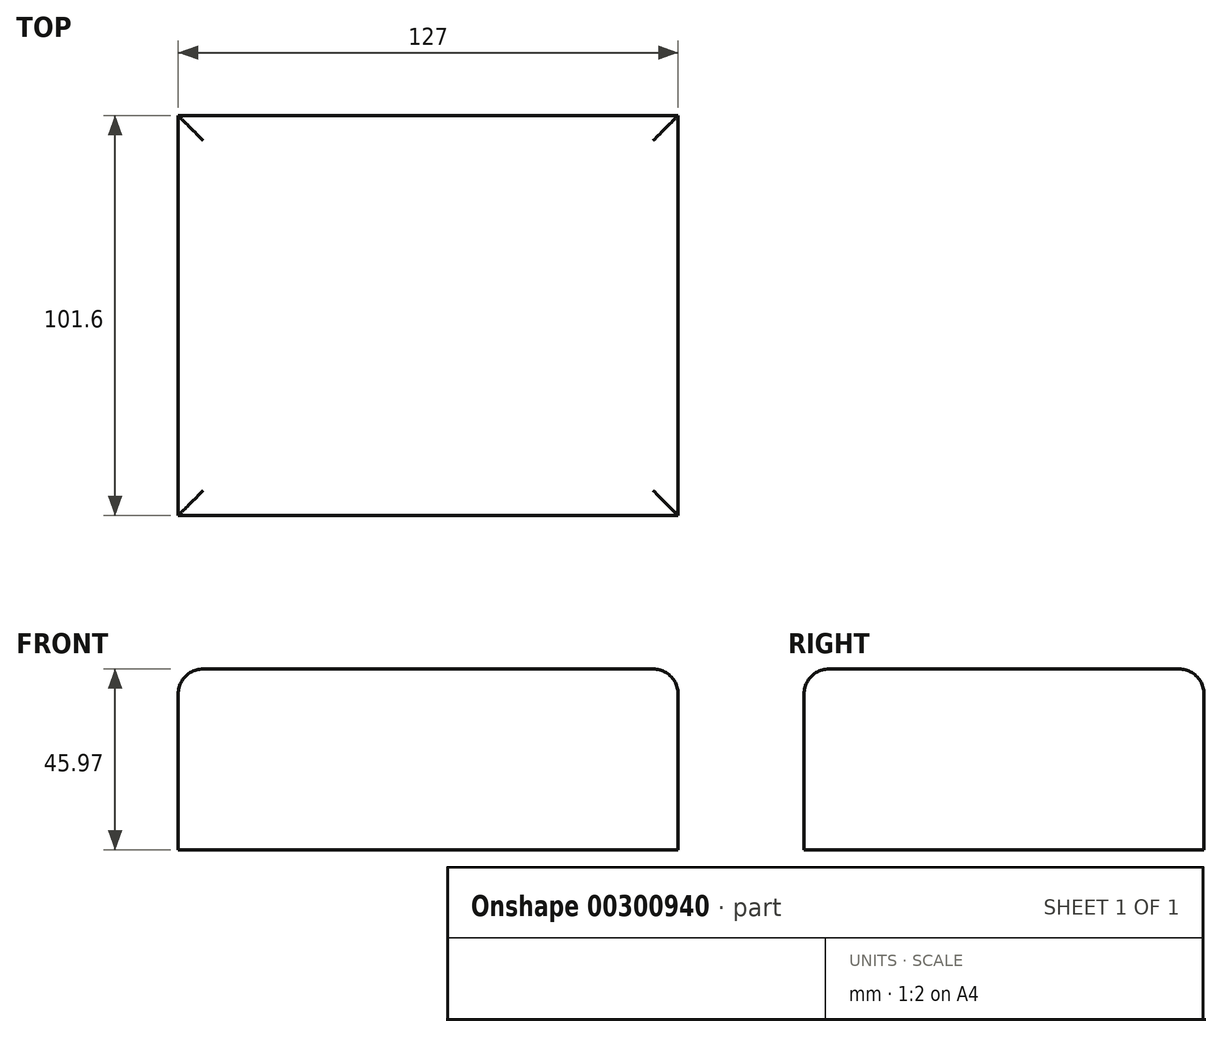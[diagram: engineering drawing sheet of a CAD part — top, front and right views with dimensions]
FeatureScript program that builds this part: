
annotation { "Feature Type Name" : "Feature", "Feature Type Description" : "" }
export const myFeature = defineFeature(function(context is Context, id is Id, definition is map)
    precondition{}
    {
        {
            var Q0;
            Q0=qCreatedBy(makeId("Top.planeOp"),FACE);
            var sketch = newSketch(context, id + "F0", { "sketchPlane" : qUnion([Q0])});
            skLineSegment(sketch, "E0.bottom", {"start": v(-44.65, -7.91) * mm, "end": v(82.35, -7.91) * mm});
            skLineSegment(sketch, "E0.top", {"start": v(-44.65, 93.69) * mm, "end": v(82.35, 93.69) * mm});
            skLineSegment(sketch, "E0.left", {"start": v(-44.65, -7.91) * mm, "end": v(-44.65, 93.69) * mm});
            skLineSegment(sketch, "E0.right", {"start": v(82.35, -7.91) * mm, "end": v(82.35, 93.69) * mm});
            skSolve(sketch);
        }
        {
            var Q0;
            Q0=makeQuery(id+"F0.imprint","IMPRINT",FACE,{"disambiguationData":[TD([[makeQuery(id+"F0.imprint","IMPRINT",EDGE,{"derivedFrom":sQuery(id+"F0.wireOp",EDGE,"E0.bottom")}),1.0]])]});
            extrude(context, id + "F1", {"entities" : qUnion([Q0]), "depth" : 45.97 * mm});
        }
        {
            var Q0;
            Q0=makeQuery(id+"F1.opExtrude","CAP_EDGE",EDGE,{"disambiguationData":[OSD([sQuery(id+"F0.wireOp",EDGE,"E0.bottom")])],"isStart":false});
            var Q1;
            Q1=makeQuery(id+"F1.opExtrude","CAP_EDGE",EDGE,{"disambiguationData":[OSD([sQuery(id+"F0.wireOp",EDGE,"E0.left")])],"isStart":false});
            var Q2;
            Q2=makeQuery(id+"F1.opExtrude","CAP_EDGE",EDGE,{"disambiguationData":[OSD([sQuery(id+"F0.wireOp",EDGE,"E0.top")])],"isStart":false});
            var Q3;
            Q3=makeQuery(id+"F1.opExtrude","CAP_EDGE",EDGE,{"disambiguationData":[OSD([sQuery(id+"F0.wireOp",EDGE,"E0.right")])],"isStart":false});
            fillet(context, id + "F2", {"entities" : qUnion([Q0, Q1, Q2, Q3]), "radius" : 6.35 * mm, "tangentPropagation" : true, "allowEdgeOverflow" : false});
        }
    });
